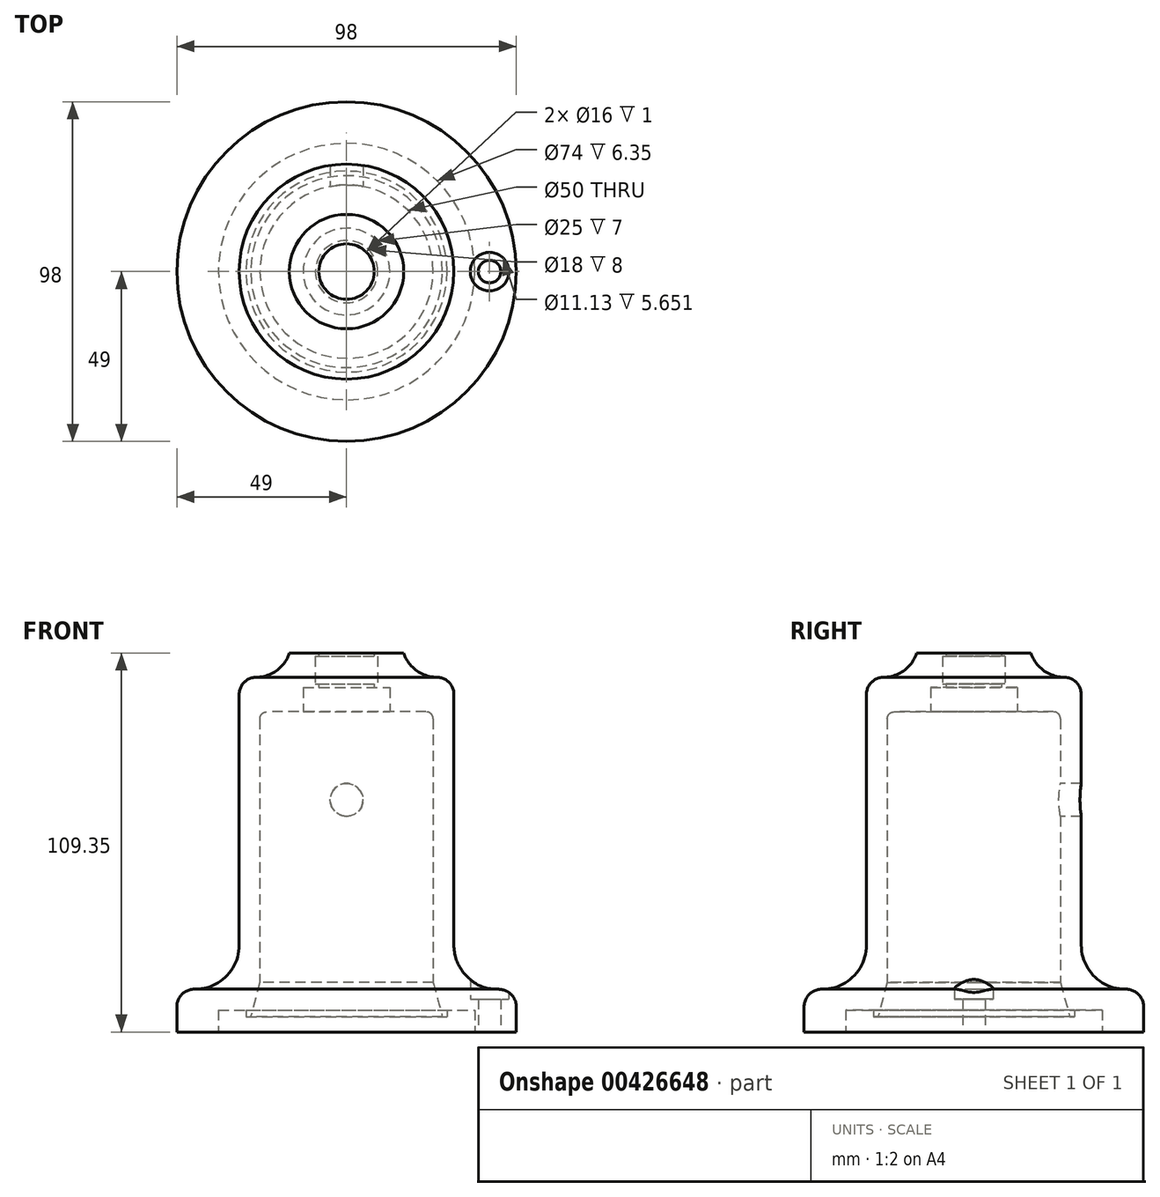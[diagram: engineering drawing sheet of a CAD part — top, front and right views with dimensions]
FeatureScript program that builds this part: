
annotation { "Feature Type Name" : "Feature", "Feature Type Description" : "" }
export const myFeature = defineFeature(function(context is Context, id is Id, definition is map)
    precondition{}
    {
        {
            var Q0;
            Q0=qCreatedBy(makeId("Right.planeOp"),FACE);
            var sketch = newSketch(context, id + "F0", { "sketchPlane" : qUnion([Q0])});
            skLineSegment(sketch, "E0", {"start": v(-25, 0) * mm, "end": v(-25, 88) * mm});
            skLineSegment(sketch, "E1", {"start": v(-25, 88) * mm, "end": v(-12.5, 88) * mm});
            skLineSegment(sketch, "E2", {"start": v(-12.5, 88) * mm, "end": v(-12.5, 95) * mm});
            skLineSegment(sketch, "E3", {"start": v(-12.5, 95) * mm, "end": v(-8, 95) * mm});
            skLineSegment(sketch, "E4", {"start": v(-8, 105) * mm, "end": v(-16.5, 105) * mm});
            skLineSegment(sketch, "E5", {"start": v(-31, 98) * mm, "end": v(-31, 8) * mm});
            skLineSegment(sketch, "E6", {"start": v(-29, 0) * mm, "end": v(-25, 0) * mm});
            skLineSegment(sketch, "E7", {"start": v(0, 0) * mm, "end": v(0, 48.4) * mm, "construction": true});
            skLineSegment(sketch, "E8", {"start": v(-31, 8) * mm, "end": v(-49, 8) * mm});
            skLineSegment(sketch, "E9", {"start": v(-49, 8) * mm, "end": v(-49, -4.35) * mm});
            skLineSegment(sketch, "E10", {"start": v(-49, -4.35) * mm, "end": v(-37, -4.35) * mm});
            skLineSegment(sketch, "E11", {"start": v(-37, -4.35) * mm, "end": v(-37, 2) * mm});
            skLineSegment(sketch, "E12", {"start": v(-37, 2) * mm, "end": v(-29, 2) * mm});
            skLineSegment(sketch, "E13", {"start": v(-29, 2) * mm, "end": v(-29, 0) * mm});
            skPoint(sketch, "E14.orphan", {"position": v(-31, 0) * mm});
            skLineSegment(sketch, "E15", {"start": v(-9, 96) * mm, "end": v(-8, 96) * mm});
            skLineSegment(sketch, "E16", {"start": v(-8, 96) * mm, "end": v(-8, 95) * mm});
            skLineSegment(sketch, "E17", {"start": v(-9, 104) * mm, "end": v(-8, 104) * mm});
            skLineSegment(sketch, "E18", {"start": v(-8, 104) * mm, "end": v(-8, 105) * mm});
            skLineSegment(sketch, "E19", {"start": v(-9, 96) * mm, "end": v(-9, 104) * mm});
            skLineSegment(sketch, "E20", {"start": v(-31, 98) * mm, "end": v(-16.5, 98) * mm});
            skLineSegment(sketch, "E21", {"start": v(-16.5, 98) * mm, "end": v(-16.5, 105) * mm});
            skSolve(sketch);
        }
        {
            var Q0;
            Q0=makeQuery(id+"F0.imprint","IMPRINT",FACE,{"disambiguationData":[TD([[makeQuery(id+"F0.imprint","IMPRINT",EDGE,{"derivedFrom":sQuery(id+"F0.wireOp",EDGE,"E0")}),1.0]])]});
            var Q1;
            Q1=sQuery(id+"F0.wireOp",EDGE,"E7");
            revolve(context, id + "F1", {"surfaceOperationType" : NewSurfaceOperationType.NEW, "entities" : qUnion([Q0]), "axis" : qUnion([Q1]), "revolveType" : RevolveType.FULL});
        }
        {
            var Q0;
            Q0=makeQuery(id+"F1.opRevolve","SWEPT_EDGE",EDGE,{"disambiguationData":[OSD([sQuery(id+"F0.wireOp",EDGE,"E5"),sQuery(id+"F0.wireOp",EDGE,"E8")])]});
            fillet(context, id + "F2", {"entities" : qUnion([Q0]), "radius" : 12.7 * mm, "tangentPropagation" : true, "allowEdgeOverflow" : false});
        }
        {
            var Q0;
            Q0=makeQuery(id+"F1.opRevolve","SWEPT_FACE",FACE,{"disambiguationData":[OSD([sQuery(id+"F0.wireOp",EDGE,"E10")])]});
            var sketch = newSketch(context, id + "F3", { "sketchPlane" : qUnion([Q0])});
            skCircle(sketch, "E22", {"center": v(41.28, 0) * mm, "radius": 3.25 * mm});
            skCircle(sketch, "E23", {"center": v(0, 0) * mm, "radius": 41.28 * mm, "construction": true});
            skSolve(sketch);
        }
        {
            var Q0;
            Q0=makeQuery(id+"F1.opRevolve","SWEPT_EDGE",EDGE,{"disambiguationData":[OSD([sQuery(id+"F0.wireOp",EDGE,"E8"),sQuery(id+"F0.wireOp",EDGE,"E9")])]});
            fillet(context, id + "F4", {"entities" : qUnion([Q0]), "radius" : 5.08 * mm, "tangentPropagation" : true, "allowEdgeOverflow" : false});
        }
        {
            var Q0;
            Q0 = qSketchRegion(id + "F3", true);
            extrude(context, id + "F5", {"entities" : qUnion([Q0]), "operationType" : NewBodyOperationType.REMOVE, "oppositeDirection" : true, "depth" : 25.4 * mm, "offsetDistance" : 25.4 * mm});
        }
        {
            var Q0;
            Q0=makeQuery(id+"F1.opRevolve","SWEPT_FACE",FACE,{"disambiguationData":[OSD([sQuery(id+"F0.wireOp",EDGE,"E10")])]});
            cPlane(context, id + "F6", {"entities" : qUnion([Q0]), "cplaneType" : CPlaneType.OFFSET, "offset" : 9.52 * mm, "oppositeDirection" : true, "width" : 152.4 * mm, "height" : 152.4 * mm});
        }
        {
            var Q0;
            Q0=qCreatedBy(id+"F6.planeOp",FACE);
            var sketch = newSketch(context, id + "F7", { "sketchPlane" : qUnion([Q0])});
            skCircle(sketch, "E24", {"center": v(41.28, 0) * mm, "radius": 5.56 * mm});
            skSolve(sketch);
        }
        {
            var Q0;
            Q0 = qSketchRegion(id + "F7", true);
            extrude(context, id + "F8", {"entities" : qUnion([Q0]), "operationType" : NewBodyOperationType.REMOVE, "oppositeDirection" : true, "depth" : 25.4 * mm, "offsetDistance" : 25.4 * mm});
        }
        {
            var Q0;
            Q0=qCreatedBy(makeId("Front.planeOp"),FACE);
            var sketch = newSketch(context, id + "F9", { "sketchPlane" : qUnion([Q0])});
            skCircle(sketch, "E25", {"center": v(0, 62.61) * mm, "radius": 4.76 * mm});
            skSolve(sketch);
        }
        {
            var Q0;
            Q0 = qSketchRegion(id + "F9", true);
            extrude(context, id + "F10", {"entities" : qUnion([Q0]), "operationType" : NewBodyOperationType.REMOVE, "endBound" : BoundingType.THROUGH_ALL, "oppositeDirection" : true, "depth" : 25.4 * mm, "offsetDistance" : 25.4 * mm});
        }
        {
            var Q0;
            Q0=makeQuery(id+"F1.opRevolve","SWEPT_EDGE",EDGE,{"disambiguationData":[OSD([sQuery(id+"F0.wireOp",EDGE,"E0"),sQuery(id+"F0.wireOp",EDGE,"E6")])]});
            chamfer(context, id + "F11", {"entities" : qUnion([Q0]), "chamferType" : ChamferType.OFFSET_ANGLE, "width" : 10 * mm, "oppositeDirection" : false, "angle" : 15 * degree, "tangentPropagation" : true});
        }
        {
            var Q0;
            Q0=makeQuery(id+"F1.opRevolve","SWEPT_EDGE",EDGE,{"disambiguationData":[OSD([sQuery(id+"F0.wireOp",EDGE,"E20"),sQuery(id+"F0.wireOp",EDGE,"E21")])]});
            fillet(context, id + "F12", {"entities" : qUnion([Q0]), "radius" : 10 * mm, "tangentPropagation" : true, "allowEdgeOverflow" : false});
        }
        {
            var Q0;
            Q0=makeQuery(id+"F1.opRevolve","SWEPT_EDGE",EDGE,{"disambiguationData":[OSD([sQuery(id+"F0.wireOp",EDGE,"E5"),sQuery(id+"F0.wireOp",EDGE,"E20")])]});
            fillet(context, id + "F13", {"entities" : qUnion([Q0]), "radius" : 5 * mm, "tangentPropagation" : true, "allowEdgeOverflow" : false});
        }
        {
            var Q0;
            Q0=makeQuery(id+"F1.opRevolve","SWEPT_EDGE",EDGE,{"disambiguationData":[OSD([sQuery(id+"F0.wireOp",EDGE,"E0"),sQuery(id+"F0.wireOp",EDGE,"E1")])]});
            fillet(context, id + "F14", {"entities" : qUnion([Q0]), "radius" : 2 * mm, "tangentPropagation" : true, "allowEdgeOverflow" : false});
        }
    });
